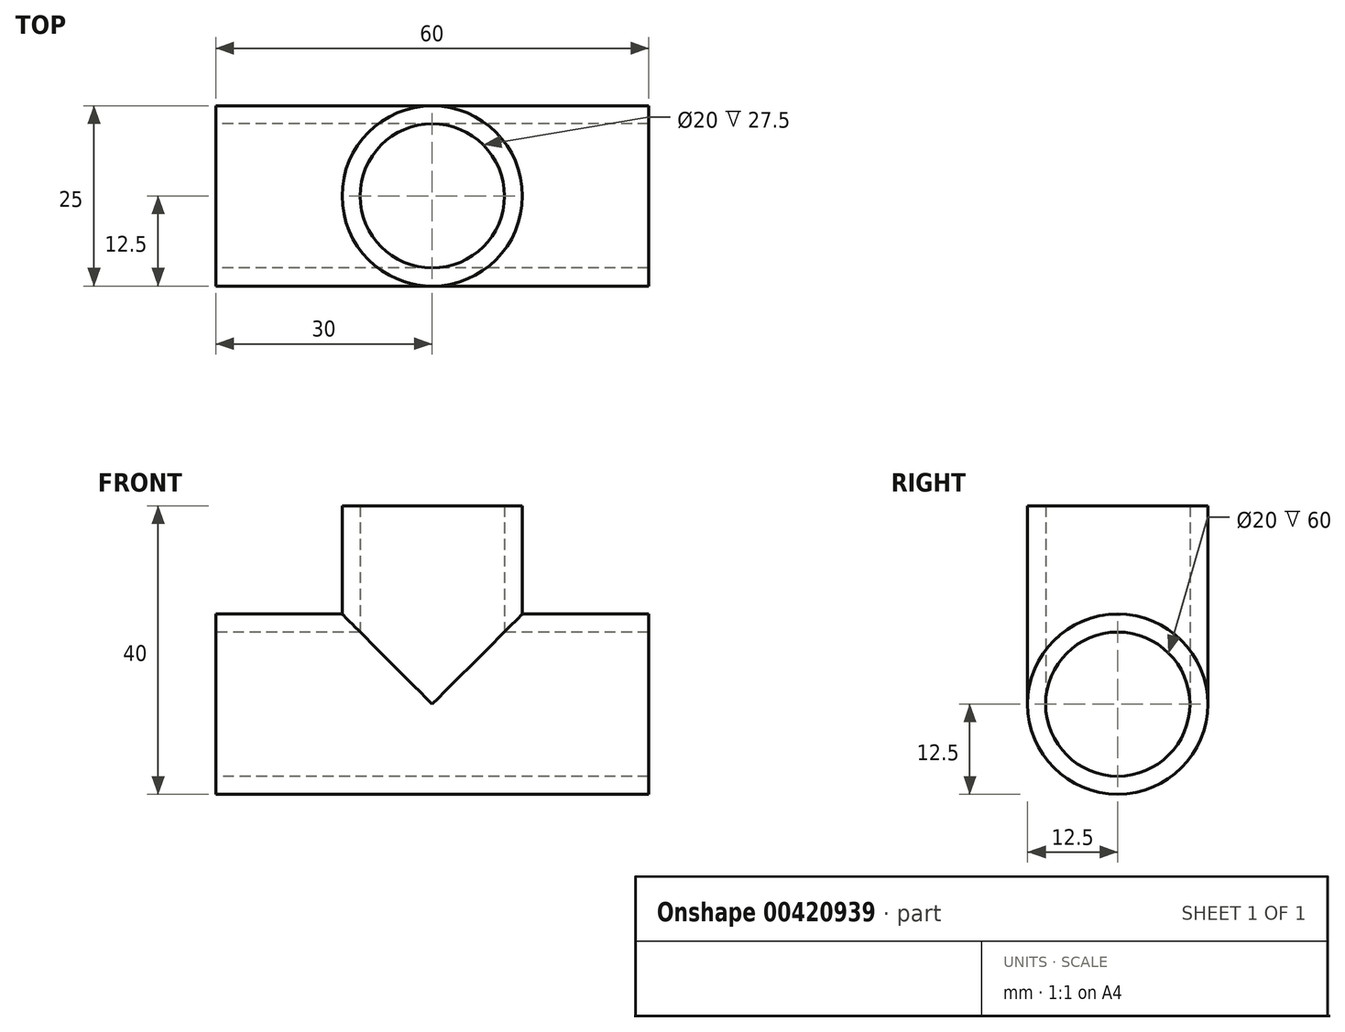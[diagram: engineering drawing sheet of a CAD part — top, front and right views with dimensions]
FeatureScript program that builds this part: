
annotation { "Feature Type Name" : "Feature", "Feature Type Description" : "" }
export const myFeature = defineFeature(function(context is Context, id is Id, definition is map)
    precondition{}
    {
        {
            var Q0;
            Q0=qCreatedBy(makeId("Right.planeOp"),FACE);
            var sketch = newSketch(context, id + "F0", { "sketchPlane" : qUnion([Q0])});
            skCircle(sketch, "E0", {"center": v(0, 0) * mm, "radius": 12.5 * mm});
            skSolve(sketch);
        }
        {
            var Q0;
            Q0 = qSketchRegion(id + "F0", true);
            extrude(context, id + "F1", {"entities" : qUnion([Q0]), "endBound" : BoundingType.SYMMETRIC, "depth" : 60 * mm});
        }
        {
            var Q0;
            Q0=qCreatedBy(makeId("Top.planeOp"),FACE);
            var sketch = newSketch(context, id + "F2", { "sketchPlane" : qUnion([Q0])});
            skCircle(sketch, "E1", {"center": v(0, 0) * mm, "radius": 12.5 * mm});
            skSolve(sketch);
        }
        {
            var Q0;
            Q0 = qSketchRegion(id + "F2", true);
            extrude(context, id + "F3", {"entities" : qUnion([Q0]), "operationType" : NewBodyOperationType.ADD, "depth" : 27.5 * mm});
        }
        {
            var Q0;
            Q0=qCreatedBy(makeId("Right.planeOp"),FACE);
            var sketch = newSketch(context, id + "F4", { "sketchPlane" : qUnion([Q0])});
            skCircle(sketch, "E2", {"center": v(0, 0) * mm, "radius": 10 * mm});
            skSolve(sketch);
        }
        {
            var Q0;
            Q0 = qSketchRegion(id + "F4", true);
            extrude(context, id + "F5", {"entities" : qUnion([Q0]), "operationType" : NewBodyOperationType.REMOVE, "endBound" : BoundingType.SYMMETRIC, "depth" : 60 * mm});
        }
        {
            var Q0;
            Q0=qCreatedBy(makeId("Top.planeOp"),FACE);
            var sketch = newSketch(context, id + "F6", { "sketchPlane" : qUnion([Q0])});
            skCircle(sketch, "E3", {"center": v(0, 0) * mm, "radius": 10 * mm});
            skSolve(sketch);
        }
        {
            var Q0;
            Q0 = qSketchRegion(id + "F6", true);
            extrude(context, id + "F7", {"entities" : qUnion([Q0]), "operationType" : NewBodyOperationType.REMOVE, "depth" : 45 * mm});
        }
    });
